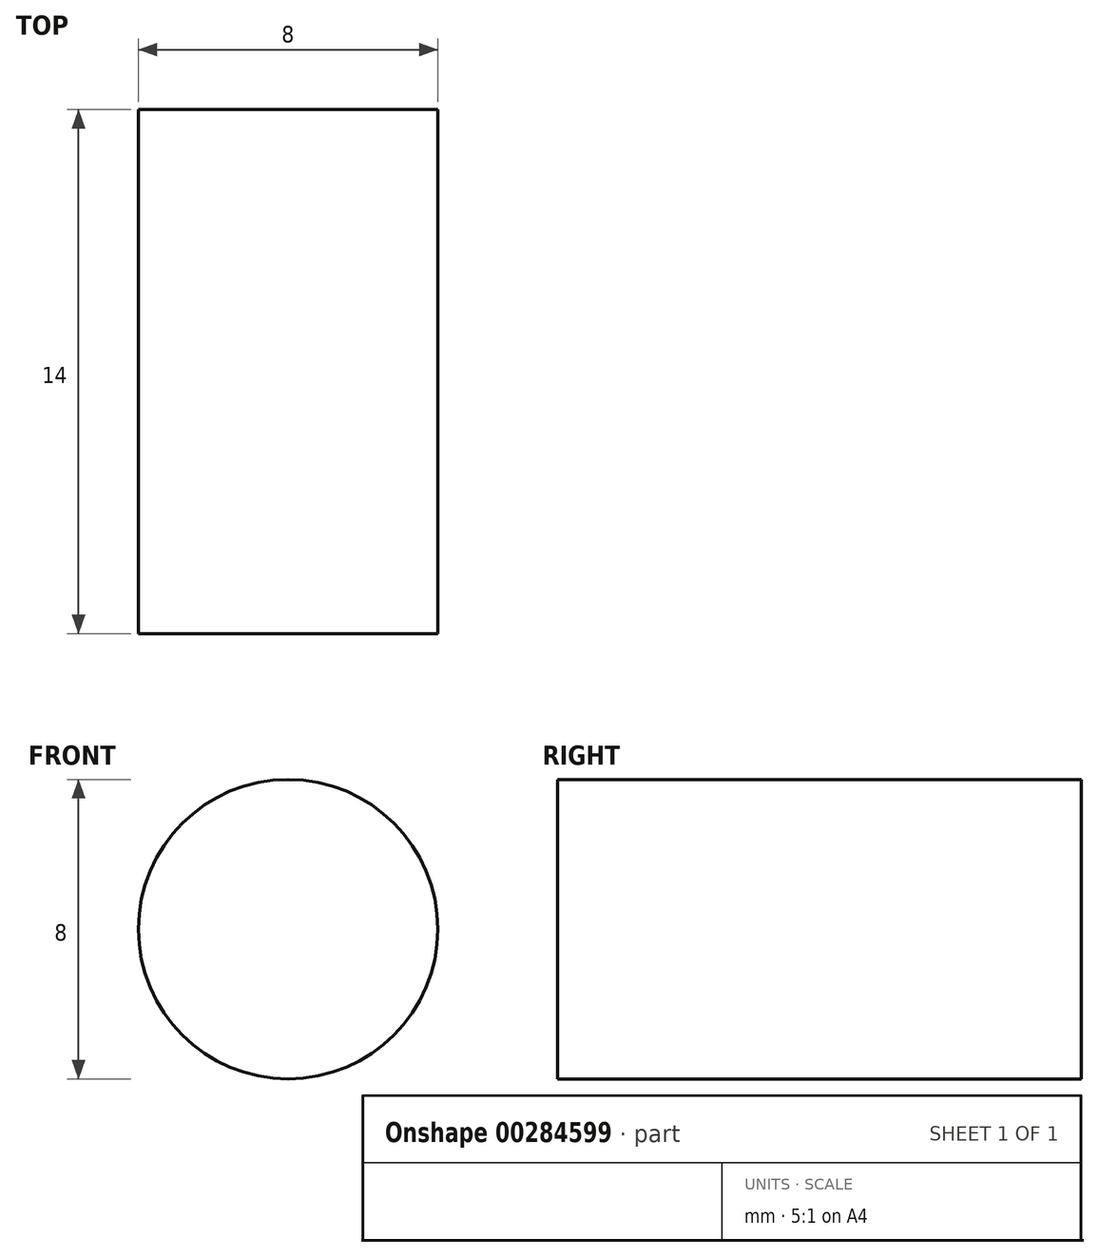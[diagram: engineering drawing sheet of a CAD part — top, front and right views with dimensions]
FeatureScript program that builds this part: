
annotation { "Feature Type Name" : "Feature", "Feature Type Description" : "" }
export const myFeature = defineFeature(function(context is Context, id is Id, definition is map)
    precondition{}
    {
        {
            var Q0;
            Q0=qCreatedBy(makeId("Front.planeOp"),FACE);
            var sketch = newSketch(context, id + "F0", { "sketchPlane" : qUnion([Q0])});
            skCircle(sketch, "E0", {"center": v(0, 0) * mm, "radius": 4 * mm});
            skSolve(sketch);
        }
        {
            var Q0;
            Q0=makeQuery(id+"F0.imprint","IMPRINT",FACE,{"disambiguationData":[TD([[makeQuery(id+"F0.imprint","IMPRINT",EDGE,{"derivedFrom":sQuery(id+"F0.wireOp",EDGE,"E0")}),1.0]])]});
            extrude(context, id + "F1", {"entities" : qUnion([Q0]), "depth" : 14 * mm});
        }
    });
